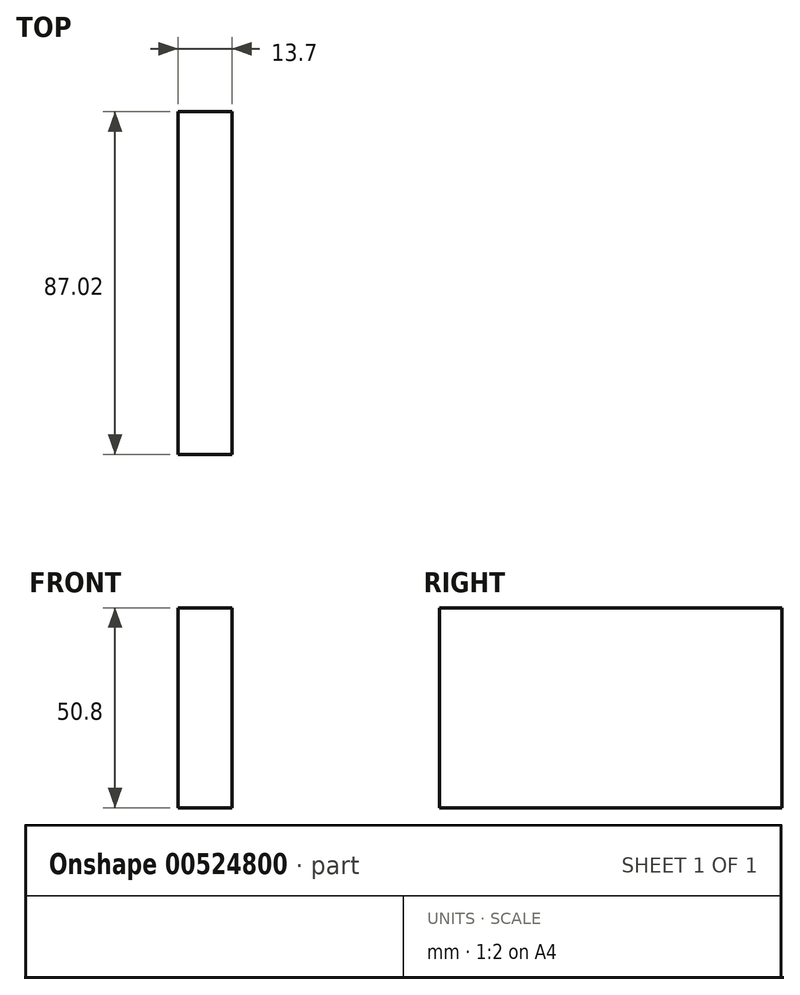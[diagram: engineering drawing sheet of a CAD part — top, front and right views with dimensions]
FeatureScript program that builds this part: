
annotation { "Feature Type Name" : "Feature", "Feature Type Description" : "" }
export const myFeature = defineFeature(function(context is Context, id is Id, definition is map)
    precondition{}
    {
        {
            var Q0;
            Q0=qCreatedBy(makeId("Top.planeOp"),FACE);
            var sketch = newSketch(context, id + "F0", { "sketchPlane" : qUnion([Q0])});
            skLineSegment(sketch, "E0.bottom", {"start": v(-47.22, 39.28) * mm, "end": v(-33.52, 39.28) * mm});
            skLineSegment(sketch, "E0.top", {"start": v(-47.22, -47.74) * mm, "end": v(-33.52, -47.74) * mm});
            skLineSegment(sketch, "E0.left", {"start": v(-47.22, 39.28) * mm, "end": v(-47.22, -47.74) * mm});
            skLineSegment(sketch, "E0.right", {"start": v(-33.52, 39.28) * mm, "end": v(-33.52, -47.74) * mm});
            skSolve(sketch);
        }
        {
            var Q0;
            Q0 = qSketchRegion(id + "F0", true);
            extrude(context, id + "F1", {"entities" : qUnion([Q0]), "depth" : 25.4 * mm, "offsetDistance" : 25.4 * mm});
        }
        {
            var Q0;
            Q0=makeQuery(id+"F1.opExtrude","SWEPT_BODY",BODY,{"disambiguationData":[OSD([sQuery(id+"F0.wireOp",EDGE,"E0.bottom"),sQuery(id+"F0.wireOp",EDGE,"E0.top"),sQuery(id+"F0.wireOp",EDGE,"E0.left"),sQuery(id+"F0.wireOp",EDGE,"E0.right")])]});
            var Q1;
            Q1=qCreatedBy(makeId("Top.planeOp"),FACE);
            mirror(context, id + "F2", {"operationType" : NewBodyOperationType.ADD, "entities" : qUnion([Q0]), "mirrorPlane" : qUnion([Q1])});
        }
    });
